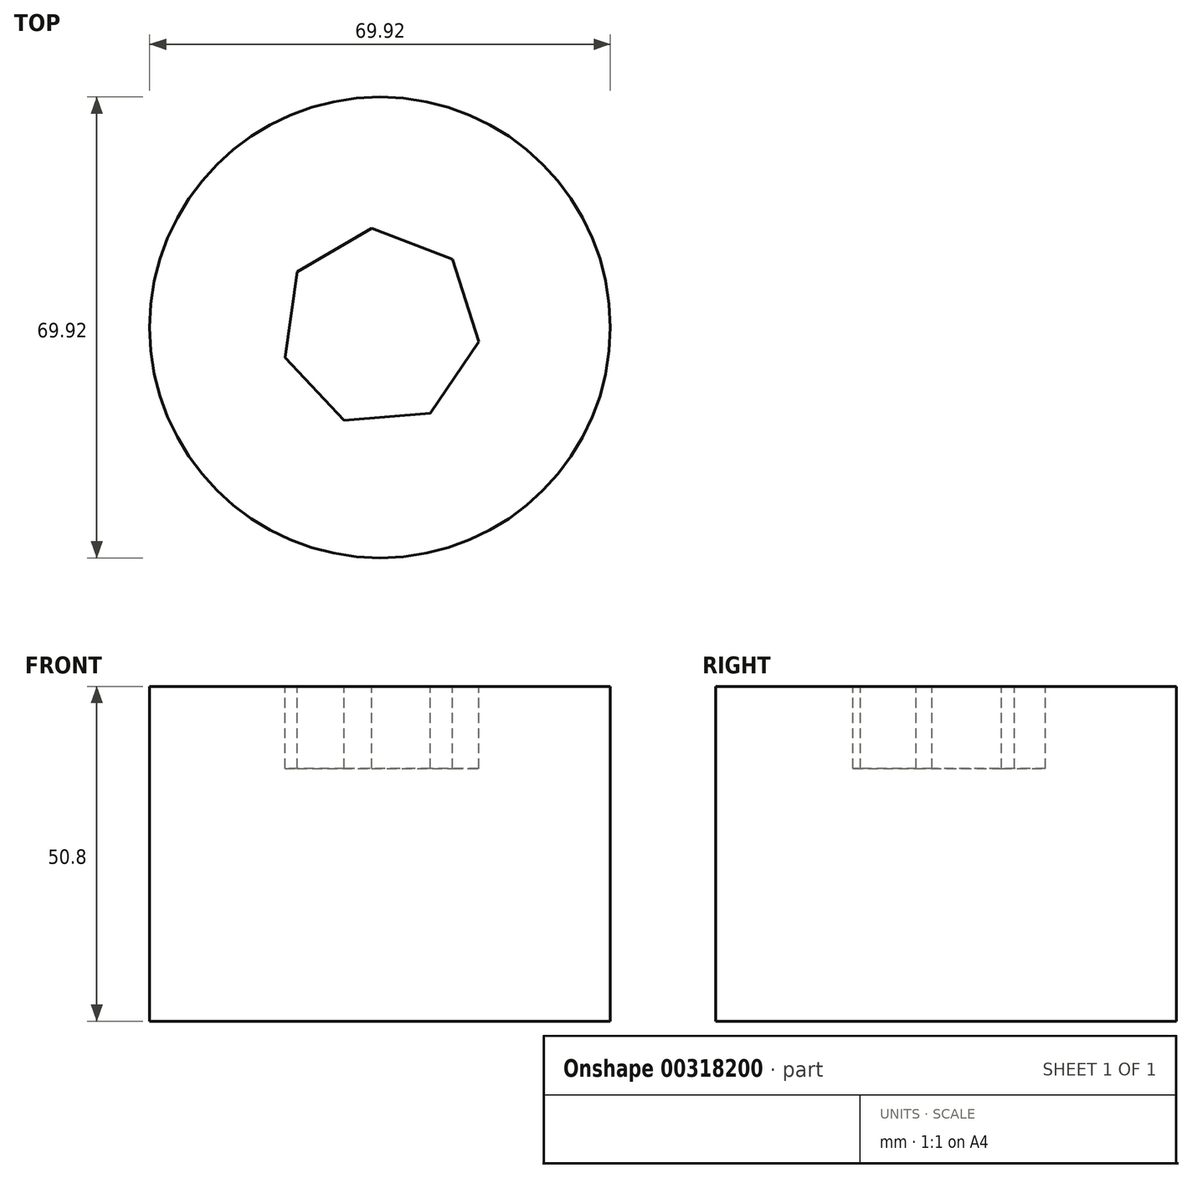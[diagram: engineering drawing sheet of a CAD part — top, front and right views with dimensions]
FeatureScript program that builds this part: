
annotation { "Feature Type Name" : "Feature", "Feature Type Description" : "" }
export const myFeature = defineFeature(function(context is Context, id is Id, definition is map)
    precondition{}
    {
        {
            var Q0;
            Q0=qCreatedBy(makeId("Top.planeOp"),FACE);
            var sketch = newSketch(context, id + "F0", { "sketchPlane" : qUnion([Q0])});
            skCircle(sketch, "E0", {"center": v(0, 0) * mm, "radius": 34.96 * mm});
            skSolve(sketch);
        }
        {
            var Q0;
            Q0 = qSketchRegion(id + "F0", true);
            extrude(context, id + "F1", {"entities" : qUnion([Q0]), "depth" : 50.8 * mm});
        }
        {
            var Q0;
            Q0=makeQuery(id+"F1.opExtrude","CAP_FACE",FACE,{"disambiguationData":[OSD([sQuery(id+"F0.wireOp",EDGE,"E0")])],"isStart":false});
            var sketch = newSketch(context, id + "F2", { "sketchPlane" : qUnion([Q0])});
            skCircle(sketch, "E1.cCircle", {"center": v(0, 0) * mm, "radius": 13.63 * mm, "construction": true});
            skLineSegment(sketch, "E1.0", {"start": v(-1.25, 15.07) * mm, "end": v(11, 10.38) * mm});
            skLineSegment(sketch, "E1.1", {"start": v(11, 10.38) * mm, "end": v(14.97, -2.13) * mm});
            skLineSegment(sketch, "E1.2", {"start": v(14.97, -2.13) * mm, "end": v(7.67, -13.03) * mm});
            skLineSegment(sketch, "E1.3", {"start": v(7.67, -13.03) * mm, "end": v(-5.4, -14.12) * mm});
            skLineSegment(sketch, "E1.4", {"start": v(-5.4, -14.12) * mm, "end": v(-14.41, -4.58) * mm});
            skLineSegment(sketch, "E1.5", {"start": v(-14.41, -4.58) * mm, "end": v(-12.57, 8.42) * mm});
            skLineSegment(sketch, "E1.6", {"start": v(-12.57, 8.42) * mm, "end": v(-1.25, 15.07) * mm});
            skPoint(sketch, "E1.0.midPoint", {"position": v(4.87, 12.72) * mm});
            skSolve(sketch);
        }
        {
            var Q0;
            Q0 = qSketchRegion(id + "F2", true);
            extrude(context, id + "F3", {"entities" : qUnion([Q0]), "operationType" : NewBodyOperationType.REMOVE, "oppositeDirection" : true, "depth" : 12.45 * mm});
        }
    });
